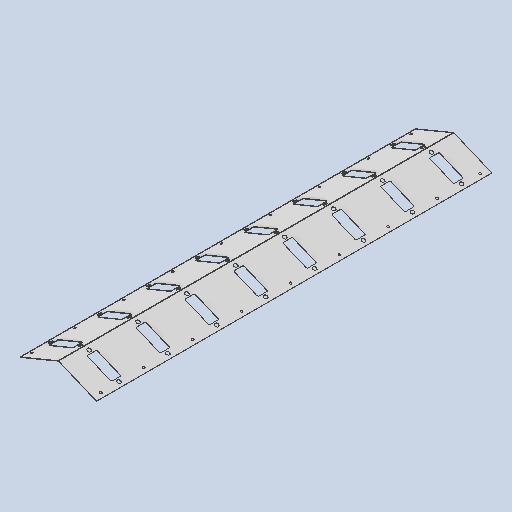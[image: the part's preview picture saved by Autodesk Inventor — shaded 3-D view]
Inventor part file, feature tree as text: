
AUTODESK INVENTOR PART (.ipt)
format: ipt  version: 2025 (Build 290162010, 162A)  size: 730,112 bytes
history: native  units: mm
features: sketch x4, sheet_metal_op x3, extrude x3, other x3, pattern_linear x2, fillet x1, pattern_circular x1, mirror x1, chamfer x1
ambient origin geometry x8: Origin, YZ Plane, XZ Plane, XY Plane, X Axis, Y Axis, Z Axis, Center Point
bodies: Body1 (feature_tree)
feature tree (19):
  sheet_metal_op  "Contour Flange2"
  extrude  "Extrusion5"  Depth=0.9mm
  extrude  "Extrusion7"  Depth=2.0mm
  fillet  "Fillet2"  Radius=2.0mm
  pattern_circular  "Circular Pattern1"  [2 undecoded]
  pattern_linear  "Rectangular Pattern5"  Count1=202  [1 undecoded]
  extrude  "Extrusion8"  Depth=2.0mm
  pattern_linear  "Rectangular Pattern6"  Spacing1=3.0mm  [1 undecoded]
  mirror  "Mirror5"
  other  "Corner Chamfer1"
  chamfer  "Corner Round1"
  sketch  "Sketch1"  dims[d46=513.0mm d47=0.9mm]
  other  "Plate4"
  sheet_metal_op  "Bend4"
  sheet_metal_op  "Corner4"
  sketch  "Sketch12"  dims[d48=4.0mm d49=2.0mm d50=2.0mm]
  sketch  "Sketch14"  dims[d51=1.0mm]
  sketch  "Sketch15"  dims[d52=4.0mm d53=2.0mm d54=2020.0mm d55=2.0mm d56=3.0mm d57=8.0mm d58=2.0mm d59=2.0mm d115=11.0mm d116=189.129mm d117=40.75mm d118=11.0mm d119=189.129mm d120=40.75mm d121=10.0mm d122=0.0mm d131=135.0mm d132=50.0mm d135=125.0mm d136=104.589mm d137=10.0mm d138=0.0mm d139=5.0mm d140=20.0mm d141=45.0deg d143=80.0mm d145=250.0mm d146=11.0mm d147=189.129mm d148=0.0mm d149=0.0mm d150=70.0mm d152=250.0mm d153=2.0mm d154=6.0mm d155=45.0deg d156=2.0mm d160=165.0mm d161=16.8mm d162=16.8mm]
  other  "Definition1"
note: 4 required parameter values undecoded (feature->parameter linkage not recoverable at this tier; creation-order binding heuristic only, values carry confidence <= 0.55)
